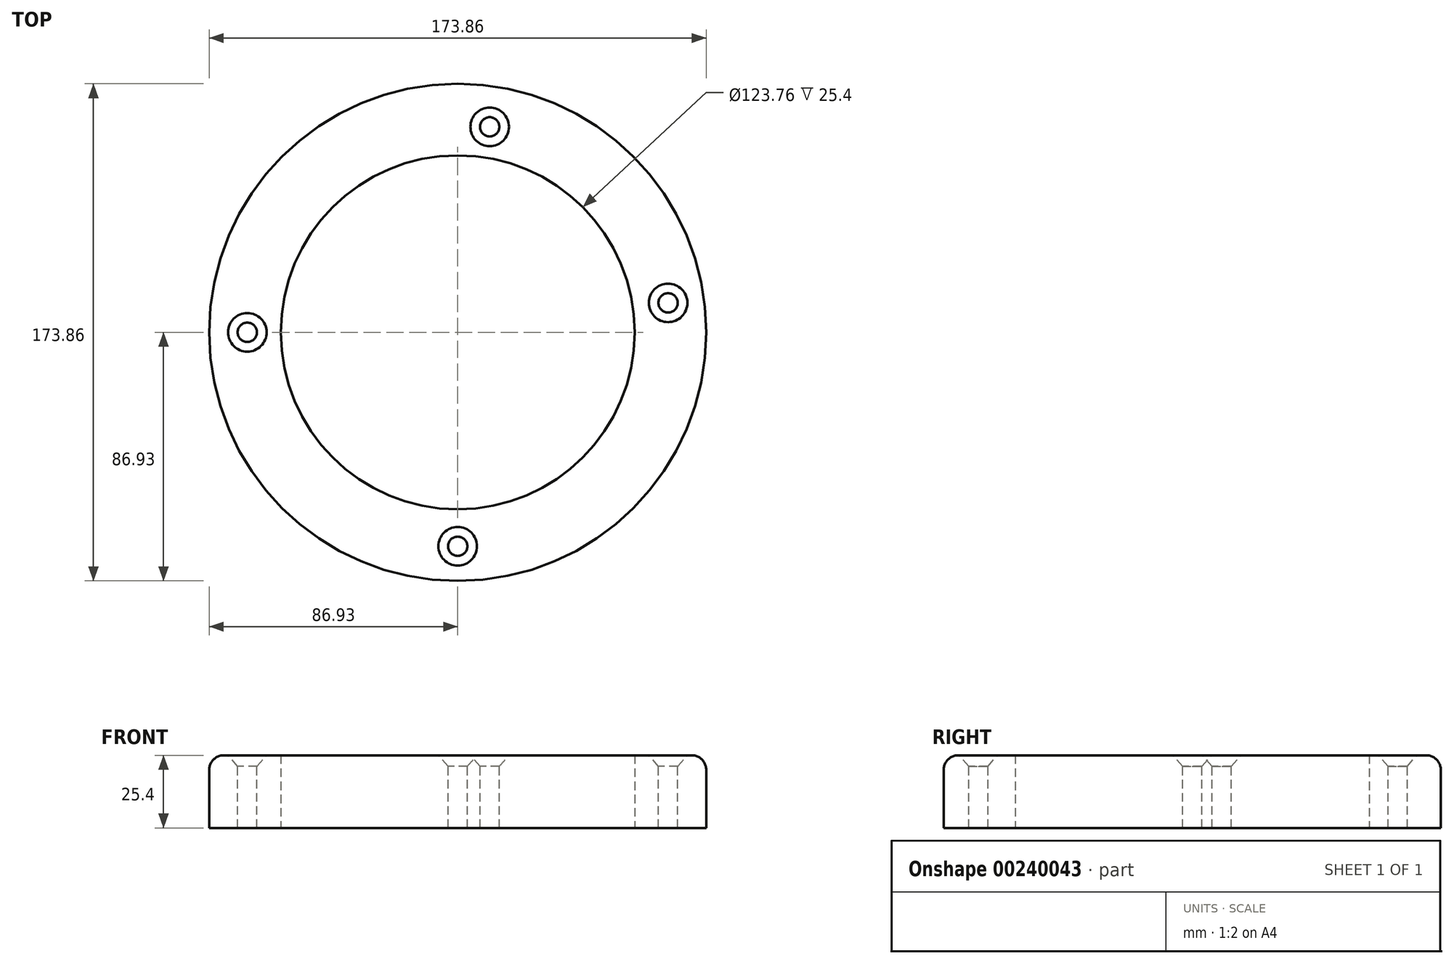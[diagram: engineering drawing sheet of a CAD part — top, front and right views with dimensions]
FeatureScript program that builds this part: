
annotation { "Feature Type Name" : "Feature", "Feature Type Description" : "" }
export const myFeature = defineFeature(function(context is Context, id is Id, definition is map)
    precondition{}
    {
        {
            var Q0;
            Q0=qCreatedBy(makeId("Top.planeOp"),FACE);
            var sketch = newSketch(context, id + "F0", { "sketchPlane" : qUnion([Q0])});
            skCircle(sketch, "E0", {"center": v(0, 0) * mm, "radius": 86.93 * mm});
            skCircle(sketch, "E1", {"center": v(0, 0) * mm, "radius": 61.88 * mm});
            skSolve(sketch);
        }
        {
            var Q0;
            Q0=makeQuery(id+"F0.imprint","IMPRINT",FACE,{"disambiguationData":[TD([[makeQuery(id+"F0.imprint","IMPRINT",EDGE,{"derivedFrom":sQuery(id+"F0.wireOp",EDGE,"E0")}),1.0]])]});
            extrude(context, id + "F1", {"entities" : qUnion([Q0]), "depth" : 25.4 * mm});
        }
        {
            var Q0;
            Q0=makeQuery(id+"F1.opExtrude","CAP_FACE",FACE,{"disambiguationData":[OSD([sQuery(id+"F0.wireOp",EDGE,"E0"),sQuery(id+"F0.wireOp",EDGE,"E1")])],"isStart":false});
            var sketch = newSketch(context, id + "F2", { "sketchPlane" : qUnion([Q0])});
            skPoint(sketch, "E2", {"position": v(-73.6, 0) * mm});
            skPoint(sketch, "E3", {"position": v(73.6, 10.3) * mm});
            skPoint(sketch, "E4", {"position": v(0, -74.83) * mm});
            skPoint(sketch, "E5", {"position": v(11.2, 71.86) * mm});
            skSolve(sketch);
        }
        {
            var Q0;
            Q0=sQuery(id+"F2.wireOp",VERTEX,"E2");
            var Q1;
            Q1=sQuery(id+"F2.wireOp",VERTEX,"E4");
            var Q2;
            Q2=sQuery(id+"F2.wireOp",VERTEX,"E3");
            var Q3;
            Q3=sQuery(id+"F2.wireOp",VERTEX,"E5");
            var Q4;
            Q4=makeQuery(id+"F1.opExtrude","SWEPT_BODY",BODY,{"disambiguationData":[OSD([sQuery(id+"F0.wireOp",EDGE,"E0"),sQuery(id+"F0.wireOp",EDGE,"E1")])]});
            hole(context, id + "F3", {"style" : HoleStyle.C_SINK, "endStyle" : HoleEndStyle.THROUGH, "holeDiameter" : 6.76 * mm, "cSinkDiameter" : 13.5 * mm, "cSinkAngle" : 82 * degree, "startFromSketch" : true, "locations" : qUnion([Q0, Q1, Q2, Q3]), "scope" : qUnion([Q4]), "isTappedThrough" : true});
        }
        {
            var Q0;
            Q0=makeQuery(id+"F1.opExtrude","CAP_EDGE",EDGE,{"disambiguationData":[OSD([sQuery(id+"F0.wireOp",EDGE,"E0")])],"isStart":false});
            fillet(context, id + "F4", {"entities" : qUnion([Q0]), "radius" : 5.08 * mm, "tangentPropagation" : true, "allowEdgeOverflow" : false});
        }
    });
